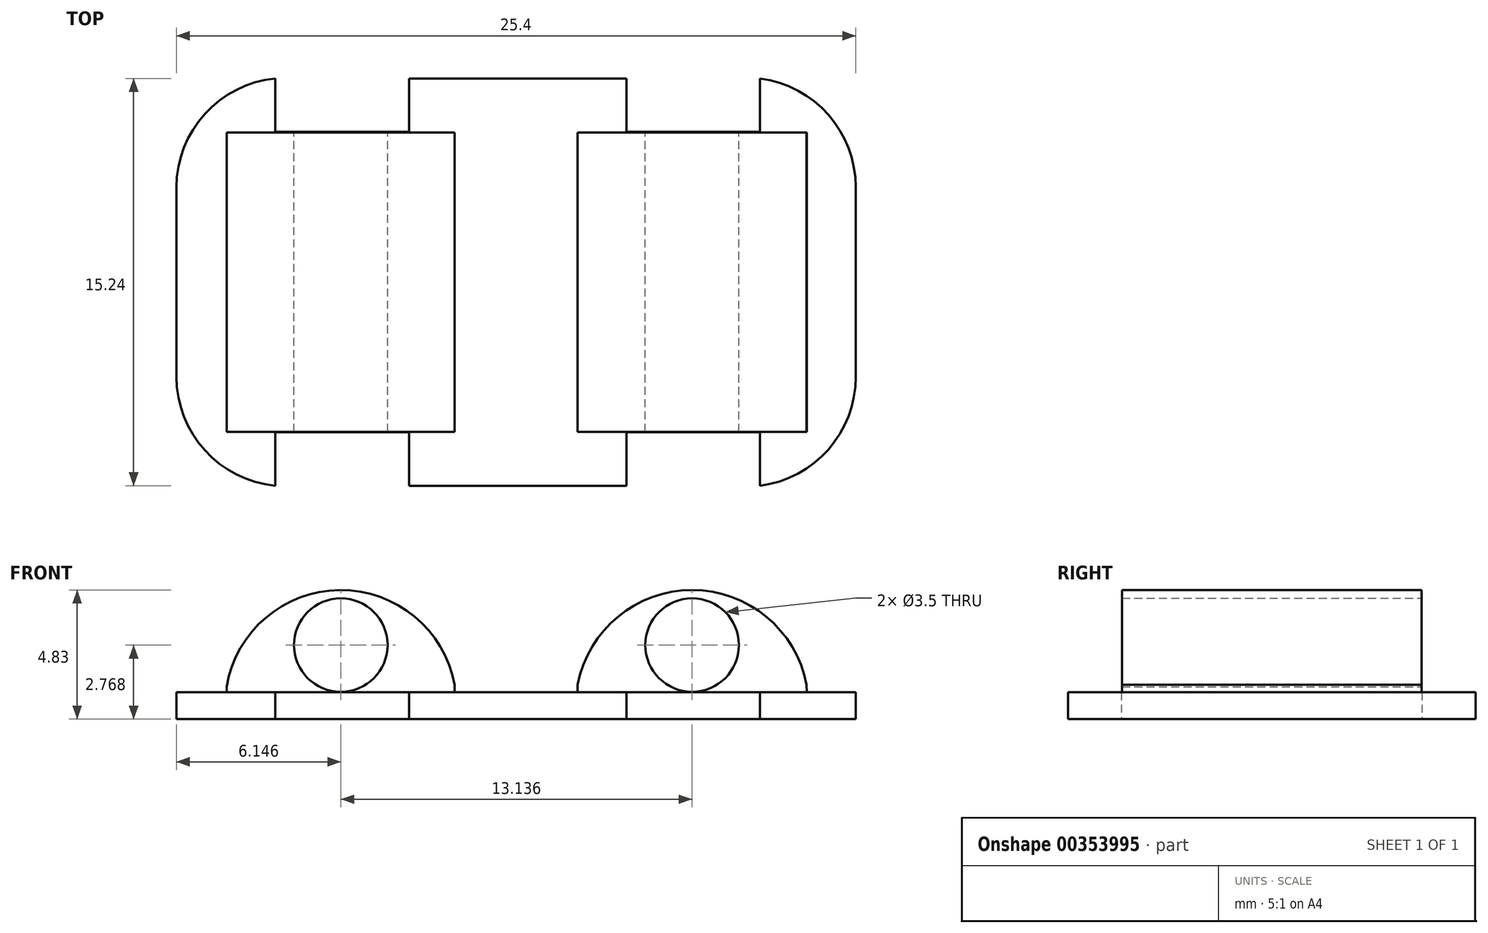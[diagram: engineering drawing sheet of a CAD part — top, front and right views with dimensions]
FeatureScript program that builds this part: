
annotation { "Feature Type Name" : "Feature", "Feature Type Description" : "" }
export const myFeature = defineFeature(function(context is Context, id is Id, definition is map)
    precondition{}
    {
        {
            var Q0;
            Q0=qCreatedBy(makeId("Top.planeOp"),FACE);
            var sketch = newSketch(context, id + "F0", { "sketchPlane" : qUnion([Q0])});
            skLineSegment(sketch, "E0.bottom", {"start": v(12.7, 7.62) * mm, "end": v(9.12, 7.62) * mm});
            skLineSegment(sketch, "E0.top", {"start": v(12.7, -7.62) * mm, "end": v(9.12, -7.62) * mm});
            skLineSegment(sketch, "E0.left", {"start": v(12.7, 7.62) * mm, "end": v(12.7, -7.62) * mm});
            skLineSegment(sketch, "E0.right", {"start": v(-12.7, 7.62) * mm, "end": v(-12.7, -7.62) * mm});
            skPoint(sketch, "E0.middle", {"position": v(0, 0) * mm});
            skLineSegment(sketch, "E1.top", {"start": v(-9, 5.62) * mm, "end": v(-4, 5.62) * mm});
            skLineSegment(sketch, "E1.left", {"start": v(-9, 7.62) * mm, "end": v(-9, 5.62) * mm});
            skLineSegment(sketch, "E1.right", {"start": v(-4, 7.62) * mm, "end": v(-4, 5.62) * mm});
            skLineSegment(sketch, "E2.bottom", {"start": v(4.12, 5.62) * mm, "end": v(9.12, 5.62) * mm});
            skLineSegment(sketch, "E2.left", {"start": v(4.12, 5.62) * mm, "end": v(4.12, 7.62) * mm});
            skLineSegment(sketch, "E2.right", {"start": v(9.12, 5.62) * mm, "end": v(9.12, 7.62) * mm});
            skLineSegment(sketch, "E3.bottom", {"start": v(-9, -5.62) * mm, "end": v(-4, -5.62) * mm});
            skLineSegment(sketch, "E3.left", {"start": v(-9, -5.62) * mm, "end": v(-9, -7.62) * mm});
            skLineSegment(sketch, "E3.right", {"start": v(-4, -5.62) * mm, "end": v(-4, -7.62) * mm});
            skLineSegment(sketch, "E4.bottom", {"start": v(9.12, -5.62) * mm, "end": v(4.12, -5.62) * mm});
            skLineSegment(sketch, "E4.left", {"start": v(9.12, -5.62) * mm, "end": v(9.12, -7.62) * mm});
            skLineSegment(sketch, "E4.right", {"start": v(4.12, -5.62) * mm, "end": v(4.12, -7.62) * mm});
            skLineSegment(sketch, "E5.trimOffspring", {"start": v(-9, 7.62) * mm, "end": v(-12.7, 7.62) * mm});
            skLineSegment(sketch, "E6.trimOffspring", {"start": v(4.12, -7.62) * mm, "end": v(-4, -7.62) * mm});
            skLineSegment(sketch, "E7.trimOffspring", {"start": v(-9, -7.62) * mm, "end": v(-12.7, -7.62) * mm});
            skLineSegment(sketch, "E8.trimOffspring", {"start": v(4.12, 7.62) * mm, "end": v(-4, 7.62) * mm});
            skSolve(sketch);
        }
        {
            var Q0;
            Q0=makeQuery(id+"F0.imprint","IMPRINT",FACE,{"disambiguationData":[TD([[makeQuery(id+"F0.imprint","IMPRINT",EDGE,{"derivedFrom":sQuery(id+"F0.wireOp",EDGE,"E0.bottom")}),1.0]])]});
            extrude(context, id + "F1", {"entities" : qUnion([Q0]), "endBound" : BoundingType.SYMMETRIC, "depth" : 1 * mm});
        }
        {
            var Q0;
            Q0=qCreatedBy(makeId("Front.planeOp"),FACE);
            var sketch = newSketch(context, id + "F2", { "sketchPlane" : qUnion([Q0])});
            skArc(sketch, "E9", {"start": v(-2.3, 0.78) * mm, "mid": v(-6.59, 4.33) * mm, "end": v(-10.82, 0.71) * mm});
            skArc(sketch, "E10", {"start": v(10.86, 0.79) * mm, "mid": v(6.58, 4.33) * mm, "end": v(2.3, 0.79) * mm});
            skPoint(sketch, "E11.centerSnap0", {"position": v(6.58, 0.79) * mm});
            skCircle(sketch, "E12", {"center": v(-6.55, 2.27) * mm, "radius": 1.75 * mm});
            skCircle(sketch, "E13", {"center": v(6.58, 2.27) * mm, "radius": 1.75 * mm});
            skLineSegment(sketch, "E14", {"start": v(2.3, 0.79) * mm, "end": v(2.3, 0) * mm});
            skLineSegment(sketch, "E15", {"start": v(2.3, 0) * mm, "end": v(10.9, 0) * mm});
            skLineSegment(sketch, "E16", {"start": v(10.9, 0) * mm, "end": v(10.86, 0.79) * mm});
            skLineSegment(sketch, "E17", {"start": v(-10.82, 0.71) * mm, "end": v(-10.82, 0) * mm});
            skLineSegment(sketch, "E18", {"start": v(-10.82, 0) * mm, "end": v(-6.55, 0) * mm});
            skLineSegment(sketch, "E19", {"start": v(-2.3, 0) * mm, "end": v(-2.3, 0.78) * mm});
            skLineSegment(sketch, "E20", {"start": v(-2.3, 0) * mm, "end": v(-6.55, 0) * mm});
            skSolve(sketch);
        }
        {
            var Q0;
            Q0=makeQuery(id+"F2.imprint","IMPRINT",FACE,{"disambiguationData":[TD([[makeQuery(id+"F2.imprint","IMPRINT",EDGE,{"derivedFrom":sQuery(id+"F2.wireOp",EDGE,"E9")}),1.0]])]});
            var Q1;
            Q1=makeQuery(id+"F2.imprint","IMPRINT",FACE,{"disambiguationData":[TD([[makeQuery(id+"F2.imprint","IMPRINT",EDGE,{"derivedFrom":sQuery(id+"F2.wireOp",EDGE,"E10")}),1.0]])]});
            extrude(context, id + "F3", {"entities" : qUnion([Q0, Q1]), "operationType" : NewBodyOperationType.ADD, "endBound" : BoundingType.SYMMETRIC, "depth" : 11.2 * mm});
        }
        {
            var Q0;
            Q0=makeQuery(id+"F1.opExtrude","SWEPT_EDGE",EDGE,{"disambiguationData":[OSD([sQuery(id+"F0.wireOp",EDGE,"E0.top"),sQuery(id+"F0.wireOp",EDGE,"E0.left")])]});
            var Q1;
            Q1=makeQuery(id+"F1.opExtrude","SWEPT_EDGE",EDGE,{"disambiguationData":[OSD([sQuery(id+"F0.wireOp",EDGE,"E0.bottom"),sQuery(id+"F0.wireOp",EDGE,"E0.left")])]});
            var Q2;
            Q2=makeQuery(id+"F1.opExtrude","SWEPT_EDGE",EDGE,{"disambiguationData":[OSD([sQuery(id+"F0.wireOp",EDGE,"E0.right"),sQuery(id+"F0.wireOp",EDGE,"E5.trimOffspring")])]});
            var Q3;
            Q3=makeQuery(id+"F1.opExtrude","SWEPT_EDGE",EDGE,{"disambiguationData":[OSD([sQuery(id+"F0.wireOp",EDGE,"E0.right"),sQuery(id+"F0.wireOp",EDGE,"E7.trimOffspring")])]});
            fillet(context, id + "F4", {"entities" : qUnion([Q0, Q1, Q2, Q3]), "radius" : 4.1 * mm, "tangentPropagation" : true, "allowEdgeOverflow" : false});
        }
    });
